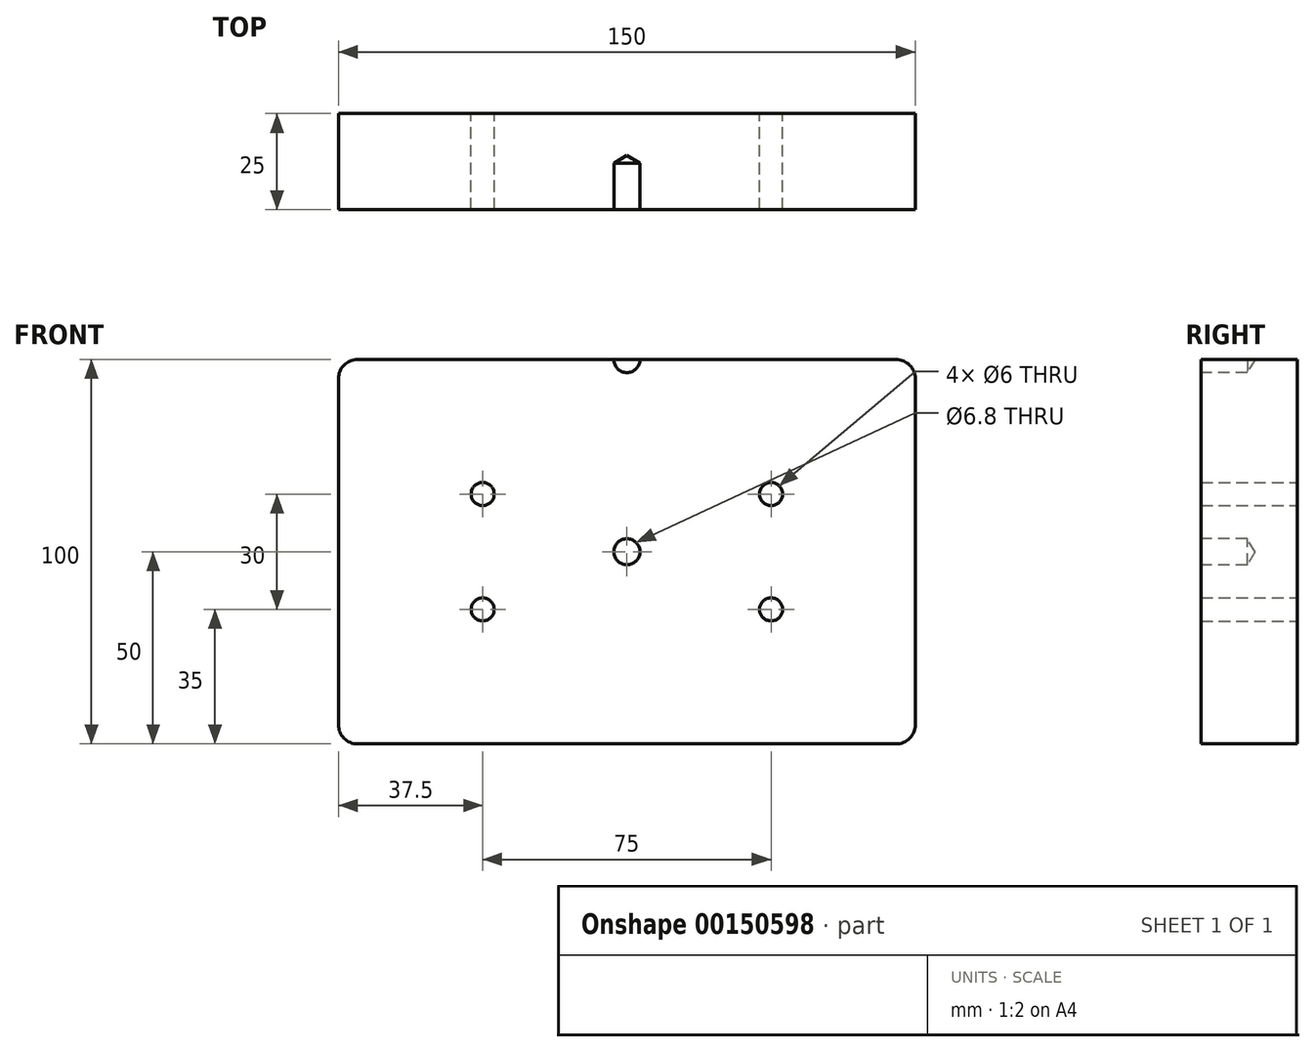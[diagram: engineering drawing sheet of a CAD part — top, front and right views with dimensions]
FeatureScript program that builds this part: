
annotation { "Feature Type Name" : "Feature", "Feature Type Description" : "" }
export const myFeature = defineFeature(function(context is Context, id is Id, definition is map)
    precondition{}
    {
        {
            var Q0;
            Q0=qCreatedBy(makeId("Front.planeOp"),FACE);
            var sketch = newSketch(context, id + "F0", { "sketchPlane" : qUnion([Q0])});
            skLineSegment(sketch, "E0.bottom", {"start": v(-70, 50) * mm, "end": v(70, 50) * mm});
            skLineSegment(sketch, "E0.top", {"start": v(-70, -50) * mm, "end": v(70, -50) * mm});
            skLineSegment(sketch, "E0.left", {"start": v(-75, 45) * mm, "end": v(-75, -45) * mm});
            skLineSegment(sketch, "E0.right", {"start": v(75, 45) * mm, "end": v(75, -45) * mm});
            skCircle(sketch, "E1", {"center": v(-37.5, 15) * mm, "radius": 3 * mm});
            skCircle(sketch, "E2", {"center": v(37.5, 15) * mm, "radius": 3 * mm});
            skCircle(sketch, "E3", {"center": v(37.5, -15) * mm, "radius": 3 * mm});
            skCircle(sketch, "E4", {"center": v(-37.5, -15) * mm, "radius": 3 * mm});
            skPoint(sketch, "E5.visualSharp", {"position": v(-75, 50) * mm});
            skArc(sketch, "E5.filletArc", {"start": v(-70, 50) * mm, "mid": v(-73.54, 48.54) * mm, "end": v(-75, 45) * mm});
            skPoint(sketch, "E6.visualSharp", {"position": v(75, 50) * mm});
            skArc(sketch, "E6.filletArc", {"start": v(75, 45) * mm, "mid": v(73.54, 48.54) * mm, "end": v(70, 50) * mm});
            skPoint(sketch, "E7.visualSharp", {"position": v(-75, -50) * mm});
            skArc(sketch, "E7.filletArc", {"start": v(-75, -45) * mm, "mid": v(-73.54, -48.54) * mm, "end": v(-70, -50) * mm});
            skPoint(sketch, "E8.visualSharp", {"position": v(75, -50) * mm});
            skArc(sketch, "E8.filletArc", {"start": v(70, -50) * mm, "mid": v(73.54, -48.54) * mm, "end": v(75, -45) * mm});
            skLineSegment(sketch, "E9", {"start": v(-37.5, 15) * mm, "end": v(37.5, 15) * mm, "construction": true});
            skLineSegment(sketch, "E10", {"start": v(37.5, -15) * mm, "end": v(37.5, 15) * mm, "construction": true});
            skLineSegment(sketch, "E11", {"start": v(-37.5, -15) * mm, "end": v(37.5, -15) * mm, "construction": true});
            skLineSegment(sketch, "E12", {"start": v(-37.5, 15) * mm, "end": v(-37.5, -15) * mm, "construction": true});
            skLineSegment(sketch, "E13", {"start": v(-37.5, 15) * mm, "end": v(37.5, -15) * mm, "construction": true});
            skLineSegment(sketch, "E14", {"start": v(37.5, 15) * mm, "end": v(-37.5, -15) * mm, "construction": true});
            skPoint(sketch, "E15", {"position": v(0, 0) * mm});
            skSolve(sketch);
        }
        {
            var Q0;
            Q0=makeQuery(id+"F0.imprint","IMPRINT",FACE,{"disambiguationData":[TD([[makeQuery(id+"F0.imprint","IMPRINT",EDGE,{"derivedFrom":sQuery(id+"F0.wireOp",EDGE,"E0.bottom")}),-1.0]])]});
            extrude(context, id + "F1", {"entities" : qUnion([Q0]), "depth" : 25 * mm});
        }
        {
            var Q0;
            Q0=makeQuery(id+"F1.opExtrude","CAP_FACE",FACE,{"disambiguationData":[OSD([sQuery(id+"F0.wireOp",EDGE,"E0.bottom"),sQuery(id+"F0.wireOp",EDGE,"E0.top"),sQuery(id+"F0.wireOp",EDGE,"E0.left"),sQuery(id+"F0.wireOp",EDGE,"E0.right"),sQuery(id+"F0.wireOp",EDGE,"E1"),sQuery(id+"F0.wireOp",EDGE,"E2"),sQuery(id+"F0.wireOp",EDGE,"E3"),sQuery(id+"F0.wireOp",EDGE,"E4"),sQuery(id+"F0.wireOp",EDGE,"E5.filletArc"),sQuery(id+"F0.wireOp",EDGE,"E6.filletArc"),sQuery(id+"F0.wireOp",EDGE,"E7.filletArc"),sQuery(id+"F0.wireOp",EDGE,"E8.filletArc")])],"isStart":false});
            var sketch = newSketch(context, id + "F2", { "sketchPlane" : qUnion([Q0])});
            skLineSegment(sketch, "E16", {"start": v(-70, 50) * mm, "end": v(70, -50) * mm, "construction": true});
            skPoint(sketch, "E17", {"position": v(0, 50) * mm});
            skLineSegment(sketch, "E18", {"start": v(70, 50) * mm, "end": v(-70, -50) * mm, "construction": true});
            skPoint(sketch, "E19", {"position": v(0, 0) * mm});
            skSolve(sketch);
        }
        {
            var Q0;
            Q0=sQuery(id+"F2.wireOp",VERTEX,"E19");
            var Q1;
            Q1=sQuery(id+"F2.wireOp",VERTEX,"E17");
            var Q2;
            Q2=makeQuery(id+"F1.opExtrude","SWEPT_BODY",BODY,{"disambiguationData":[OSD([sQuery(id+"F0.wireOp",EDGE,"E0.bottom"),sQuery(id+"F0.wireOp",EDGE,"E0.top"),sQuery(id+"F0.wireOp",EDGE,"E0.left"),sQuery(id+"F0.wireOp",EDGE,"E0.right"),sQuery(id+"F0.wireOp",EDGE,"E1"),sQuery(id+"F0.wireOp",EDGE,"E2"),sQuery(id+"F0.wireOp",EDGE,"E3"),sQuery(id+"F0.wireOp",EDGE,"E4"),sQuery(id+"F0.wireOp",EDGE,"E5.filletArc"),sQuery(id+"F0.wireOp",EDGE,"E6.filletArc"),sQuery(id+"F0.wireOp",EDGE,"E7.filletArc"),sQuery(id+"F0.wireOp",EDGE,"E8.filletArc")])]});
            hole(context, id + "F3", {"style" : HoleStyle.SIMPLE, "endStyle" : HoleEndStyle.BLIND, "standardTappedOrClearance" : lookupTablePath({ "standard" : "ISO", "engagement" : "75%", "pitch" : "1.25 mm", "size" : "M8", "type" : "Tapped" }), "standardBlindInLast" : lookupTablePath({ "standard" : "ISO", "engagement" : "75%", "pitch" : "1.25 mm", "size" : "M8", "type" : "Tapped" }), "holeDiameter" : 6.8 * mm, "holeDepth" : 12 * mm, "locations" : qUnion([Q0, Q1]), "scope" : qUnion([Q2]), "majorDiameter" : 8 * mm});
        }
    });
